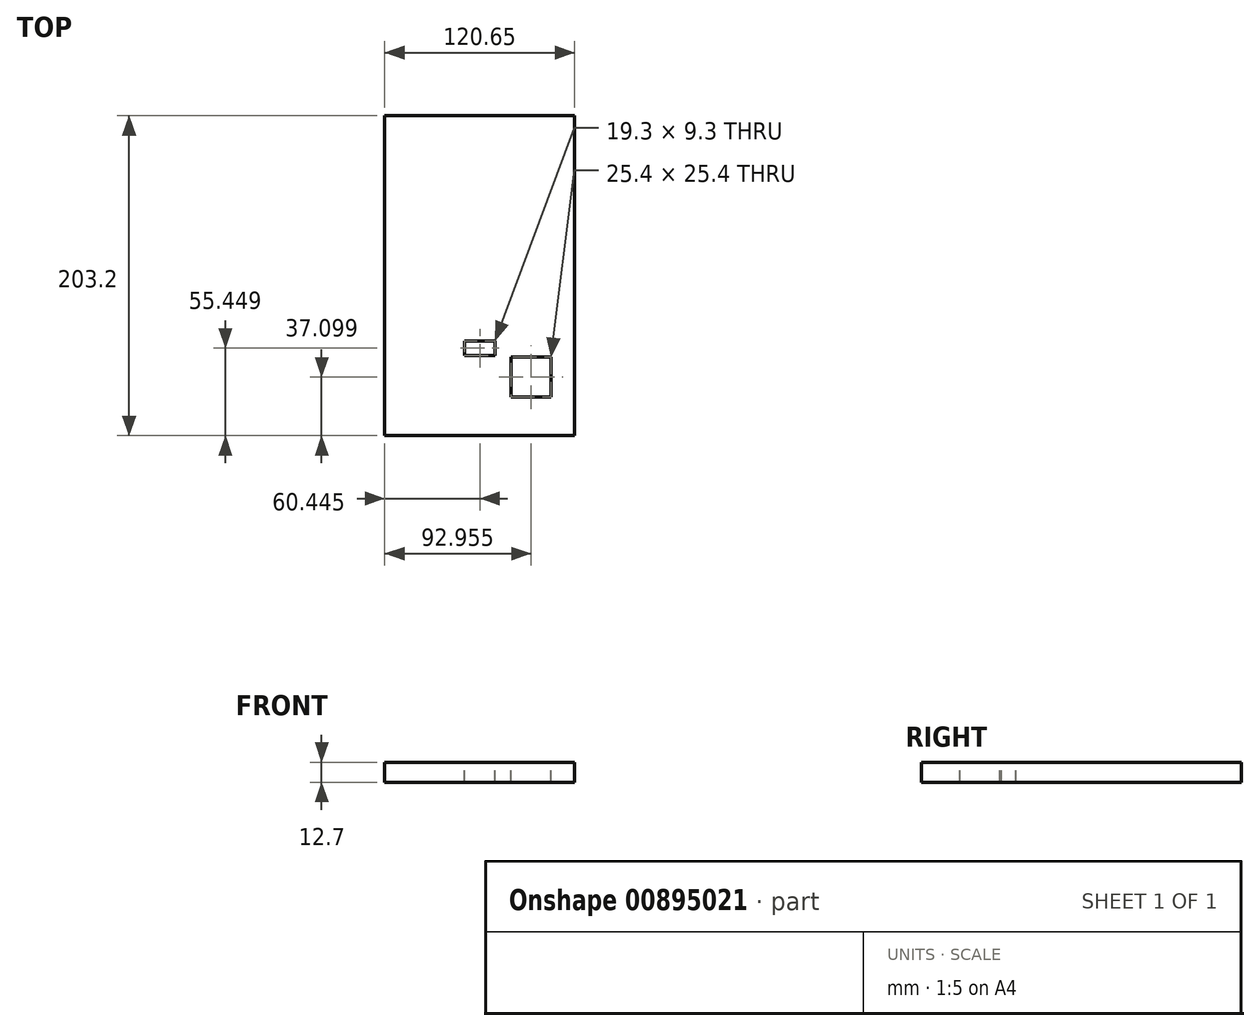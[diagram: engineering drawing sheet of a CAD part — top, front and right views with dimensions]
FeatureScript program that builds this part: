
annotation { "Feature Type Name" : "Feature", "Feature Type Description" : "" }
export const myFeature = defineFeature(function(context is Context, id is Id, definition is map)
    precondition{}
    {
        {
            var Q0;
            Q0=qCreatedBy(makeId("Top.planeOp"),FACE);
            var sketch = newSketch(context, id + "F0", { "sketchPlane" : qUnion([Q0])});
            skLineSegment(sketch, "E0.bottom", {"start": v(-46.5, 174.88) * mm, "end": v(74.16, 174.88) * mm});
            skLineSegment(sketch, "E0.top", {"start": v(-46.5, -28.32) * mm, "end": v(74.16, -28.32) * mm});
            skLineSegment(sketch, "E0.left", {"start": v(-46.5, 174.88) * mm, "end": v(-46.5, -28.32) * mm});
            skLineSegment(sketch, "E0.right", {"start": v(74.16, 174.88) * mm, "end": v(74.16, -28.32) * mm});
            skSolve(sketch);
        }
        {
            var Q0;
            Q0 = qSketchRegion(id + "F0", true);
            extrude(context, id + "F1", {"entities" : qUnion([Q0]), "depth" : 12.7 * mm, "offsetDistance" : 25.4 * mm});
        }
        {
            var Q0;
            Q0=makeQuery(id+"F1.opExtrude","CAP_FACE",FACE,{"disambiguationData":[OSD([sQuery(id+"F0.wireOp",EDGE,"E0.bottom"),sQuery(id+"F0.wireOp",EDGE,"E0.top"),sQuery(id+"F0.wireOp",EDGE,"E0.left"),sQuery(id+"F0.wireOp",EDGE,"E0.right")])],"isStart":false});
            var sketch = newSketch(context, id + "F2", { "sketchPlane" : qUnion([Q0])});
            skLineSegment(sketch, "E1.0", {"start": v(-46.5, 174.88) * mm, "end": v(-46.5, -28.32) * mm, "construction": true});
            skLineSegment(sketch, "E2.bottom", {"start": v(4.3, 31.78) * mm, "end": v(13.6, 31.78) * mm});
            skLineSegment(sketch, "E2.top", {"start": v(4.3, 22.48) * mm, "end": v(13.6, 22.48) * mm});
            skLineSegment(sketch, "E2.left", {"start": v(4.3, 31.78) * mm, "end": v(4.3, 22.48) * mm});
            skLineSegment(sketch, "E2.right", {"start": v(13.6, 31.78) * mm, "end": v(13.6, 22.48) * mm});
            skLineSegment(sketch, "E3.1.0.0", {"start": v(14.3, 31.78) * mm, "end": v(23.6, 31.78) * mm});
            skLineSegment(sketch, "E3.1.0.1", {"start": v(14.3, 31.78) * mm, "end": v(14.3, 22.48) * mm});
            skLineSegment(sketch, "E3.1.0.2", {"start": v(14.3, 22.48) * mm, "end": v(23.6, 22.48) * mm});
            skLineSegment(sketch, "E3.1.0.3", {"start": v(23.6, 31.78) * mm, "end": v(23.6, 22.48) * mm});
            skLineSegment(sketch, "E3.direction1", {"start": v(4.3, 22.48) * mm, "end": v(14.3, 22.48) * mm, "construction": true});
            skLineSegment(sketch, "E4.bottom", {"start": v(13.6, 54.16) * mm, "end": v(0.9, 54.16) * mm});
            skLineSegment(sketch, "E4.top", {"start": v(13.6, 130.36) * mm, "end": v(0.9, 130.36) * mm});
            skLineSegment(sketch, "E4.left", {"start": v(13.6, 54.16) * mm, "end": v(13.6, 130.36) * mm, "construction": true});
            skLineSegment(sketch, "E4.right", {"start": v(0.9, 54.16) * mm, "end": v(0.9, 130.36) * mm, "construction": true});
            skLineSegment(sketch, "E5.bottom", {"start": v(14.3, 54.16) * mm, "end": v(27, 54.16) * mm});
            skLineSegment(sketch, "E5.top", {"start": v(14.3, 130.36) * mm, "end": v(27, 130.36) * mm});
            skLineSegment(sketch, "E5.left", {"start": v(14.3, 54.16) * mm, "end": v(14.3, 130.36) * mm});
            skLineSegment(sketch, "E5.right", {"start": v(27, 54.16) * mm, "end": v(27, 130.36) * mm, "construction": true});
            skLineSegment(sketch, "E6", {"start": v(13.6, 31.78) * mm, "end": v(14.3, 31.78) * mm});
            skLineSegment(sketch, "E7", {"start": v(13.6, 22.48) * mm, "end": v(14.3, 22.48) * mm});
            skLineSegment(sketch, "E8", {"start": v(13.6, 130.36) * mm, "end": v(14.3, 130.36) * mm});
            skLineSegment(sketch, "E9", {"start": v(13.6, 54.16) * mm, "end": v(14.3, 54.16) * mm});
            skLineSegment(sketch, "E10.bottom", {"start": v(33.77, 21.48) * mm, "end": v(59.17, 21.48) * mm});
            skLineSegment(sketch, "E10.top", {"start": v(33.77, -3.92) * mm, "end": v(59.17, -3.92) * mm});
            skLineSegment(sketch, "E10.left", {"start": v(33.77, 21.48) * mm, "end": v(33.77, -3.92) * mm});
            skLineSegment(sketch, "E10.right", {"start": v(59.17, 21.48) * mm, "end": v(59.17, -3.92) * mm});
            skSolve(sketch);
        }
        {
            var Q0;
            Q0 = qSketchRegion(id + "F2", true);
            extrude(context, id + "F3", {"entities" : qUnion([Q0]), "operationType" : NewBodyOperationType.REMOVE, "oppositeDirection" : true, "depth" : 25.4 * mm, "offsetDistance" : 25.4 * mm});
        }
    });
